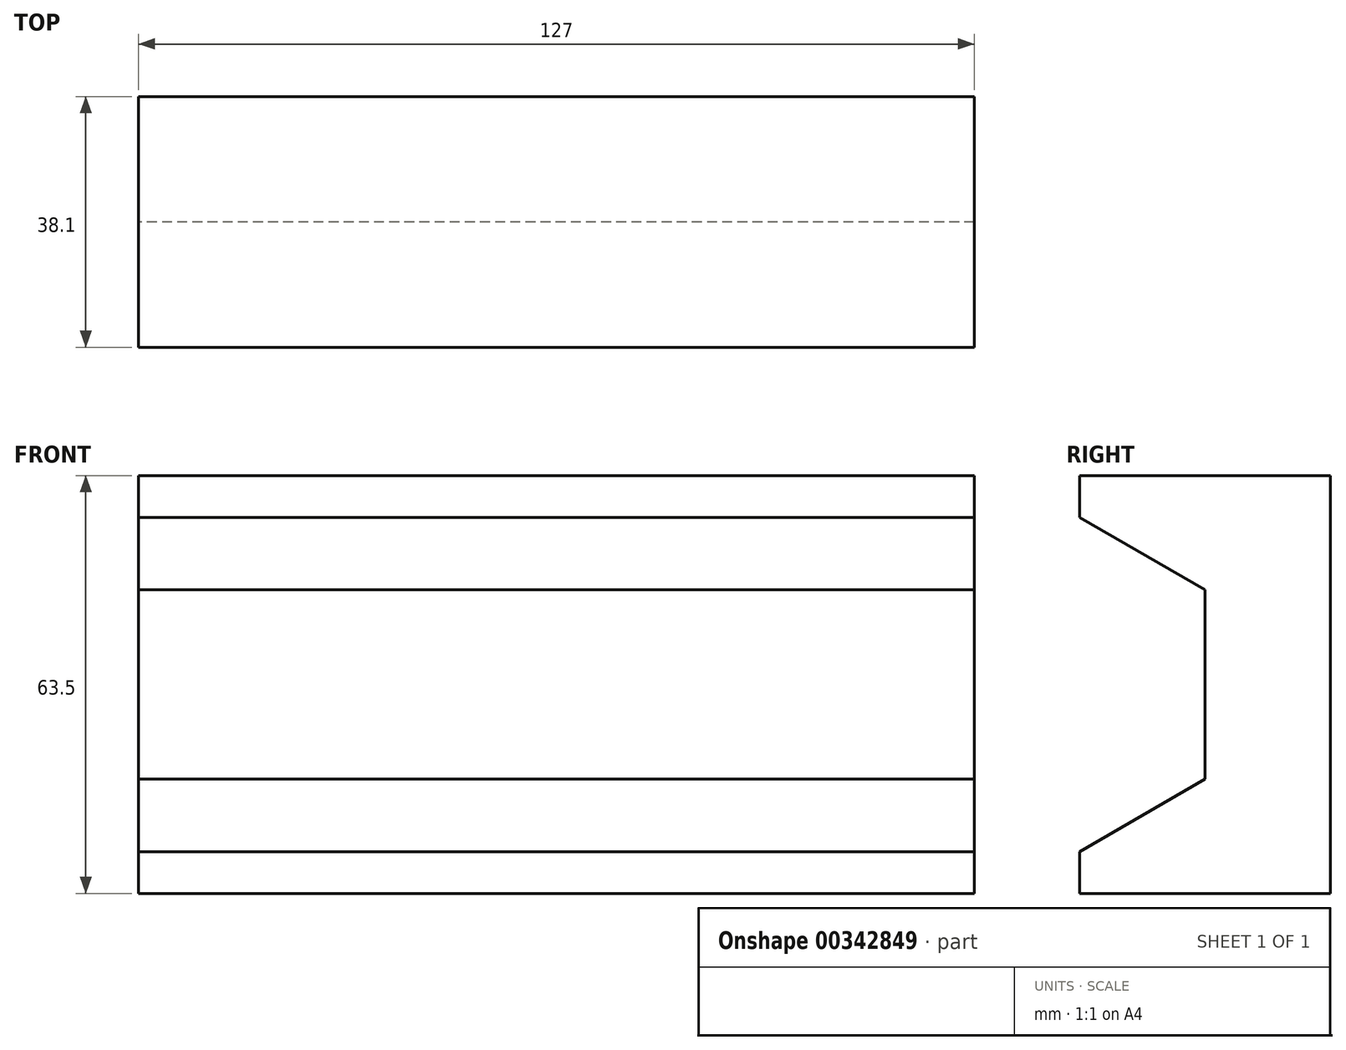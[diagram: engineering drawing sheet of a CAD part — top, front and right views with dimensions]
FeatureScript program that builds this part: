
annotation { "Feature Type Name" : "Feature", "Feature Type Description" : "" }
export const myFeature = defineFeature(function(context is Context, id is Id, definition is map)
    precondition{}
    {
        {
            var Q0;
            Q0=qCreatedBy(makeId("Right.planeOp"),FACE);
            var sketch = newSketch(context, id + "F0", { "sketchPlane" : qUnion([Q0])});
            skLineSegment(sketch, "E0.bottom", {"start": v(-19.05, -31.75) * mm, "end": v(19.05, -31.75) * mm});
            skLineSegment(sketch, "E0.top", {"start": v(-19.05, 31.75) * mm, "end": v(19.05, 31.75) * mm});
            skLineSegment(sketch, "E0.left", {"start": v(-19.05, -31.75) * mm, "end": v(-19.05, -25.4) * mm});
            skLineSegment(sketch, "E0.right", {"start": v(19.05, -31.75) * mm, "end": v(19.05, 31.75) * mm});
            skPoint(sketch, "E0.middle", {"position": v(0, 0) * mm});
            skLineSegment(sketch, "E1", {"start": v(-19.05, 31.75) * mm, "end": v(-19.05, 25.4) * mm});
            skLineSegment(sketch, "E2", {"start": v(-19.05, 25.4) * mm, "end": v(0, 14.4) * mm});
            skLineSegment(sketch, "E3", {"start": v(-19.05, -25.4) * mm, "end": v(0, -14.4) * mm});
            skLineSegment(sketch, "E4", {"start": v(0, -14.4) * mm, "end": v(0, 14.4) * mm});
            skLineSegment(sketch, "E5.trimOffspring", {"start": v(-19.05, 25.4) * mm, "end": v(-19.05, 31.75) * mm});
            skSolve(sketch);
        }
        {
            var Q0;
            Q0 = qSketchRegion(id + "F0", true);
            extrude(context, id + "F1", {"entities" : qUnion([Q0]), "depth" : 127 * mm});
        }
    });
